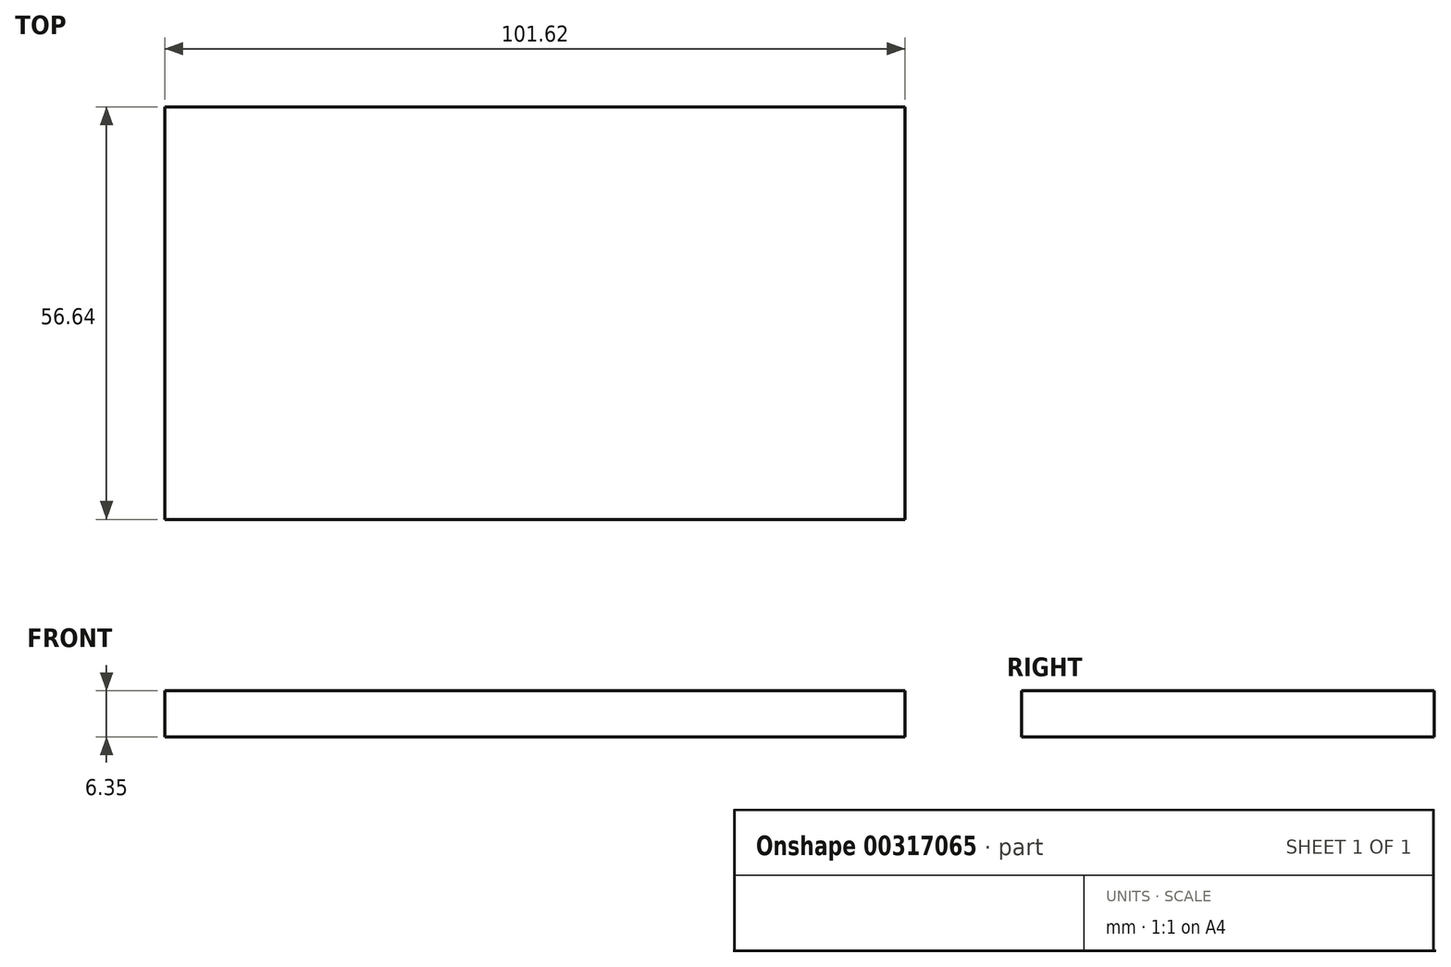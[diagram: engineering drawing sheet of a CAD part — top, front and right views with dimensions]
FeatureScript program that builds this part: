
annotation { "Feature Type Name" : "Feature", "Feature Type Description" : "" }
export const myFeature = defineFeature(function(context is Context, id is Id, definition is map)
    precondition{}
    {
        {
            var Q0;
            Q0=qCreatedBy(makeId("Top.planeOp"),FACE);
            var sketch = newSketch(context, id + "F0", { "sketchPlane" : qUnion([Q0])});
            skLineSegment(sketch, "E0.bottom", {"start": v(-50.8, 29.78) * mm, "end": v(50.8, 29.78) * mm});
            skLineSegment(sketch, "E0.top", {"start": v(-50.8, -26.86) * mm, "end": v(50.8, -26.86) * mm});
            skLineSegment(sketch, "E0.left", {"start": v(-50.8, 29.78) * mm, "end": v(-50.8, -26.86) * mm});
            skLineSegment(sketch, "E0.right", {"start": v(50.8, 29.78) * mm, "end": v(50.8, -26.86) * mm});
            skSolve(sketch);
        }
        {
            var Q0;
            Q0 = qSketchRegion(id + "F0", true);
            extrude(context, id + "F1", {"entities" : qUnion([Q0]), "depth" : 6.35 * mm});
        }
        {
            var Q0;
            Q0=makeQuery(id+"F1.opExtrude","CAP_FACE",FACE,{"disambiguationData":[OSD([sQuery(id+"F0.wireOp",EDGE,"E0.bottom"),sQuery(id+"F0.wireOp",EDGE,"E0.top"),sQuery(id+"F0.wireOp",EDGE,"E0.left"),sQuery(id+"F0.wireOp",EDGE,"E0.right")])],"isStart":false});
            var sketch = newSketch(context, id + "F2", { "sketchPlane" : qUnion([Q0])});
            skLineSegment(sketch, "E1.bottom", {"start": v(-29.65, 14.82) * mm, "end": v(16.4, 14.82) * mm});
            skLineSegment(sketch, "E1.top", {"start": v(-29.65, -10.02) * mm, "end": v(16.4, -10.02) * mm});
            skLineSegment(sketch, "E1.left", {"start": v(-29.65, 14.82) * mm, "end": v(-29.65, -10.02) * mm});
            skLineSegment(sketch, "E1.right", {"start": v(16.4, 14.82) * mm, "end": v(16.4, -10.02) * mm});
            skSolve(sketch);
        }
        {
            var Q0;
            Q0=sQuery(id+"F2.wireOp",EDGE,"E1.bottom");
            var Q1;
            Q1=sQuery(id+"F2.wireOp",EDGE,"E1.top");
            var Q2;
            Q2=sQuery(id+"F2.wireOp",EDGE,"E1.left");
            var Q3;
            Q3=sQuery(id+"F2.wireOp",EDGE,"E1.right");
            extrude(context, id + "F3", {"bodyType" : ToolBodyType.SURFACE, "surfaceEntities" : qUnion([Q0, Q1, Q2, Q3]), "depth" : 25.4 * mm});
        }
    });
